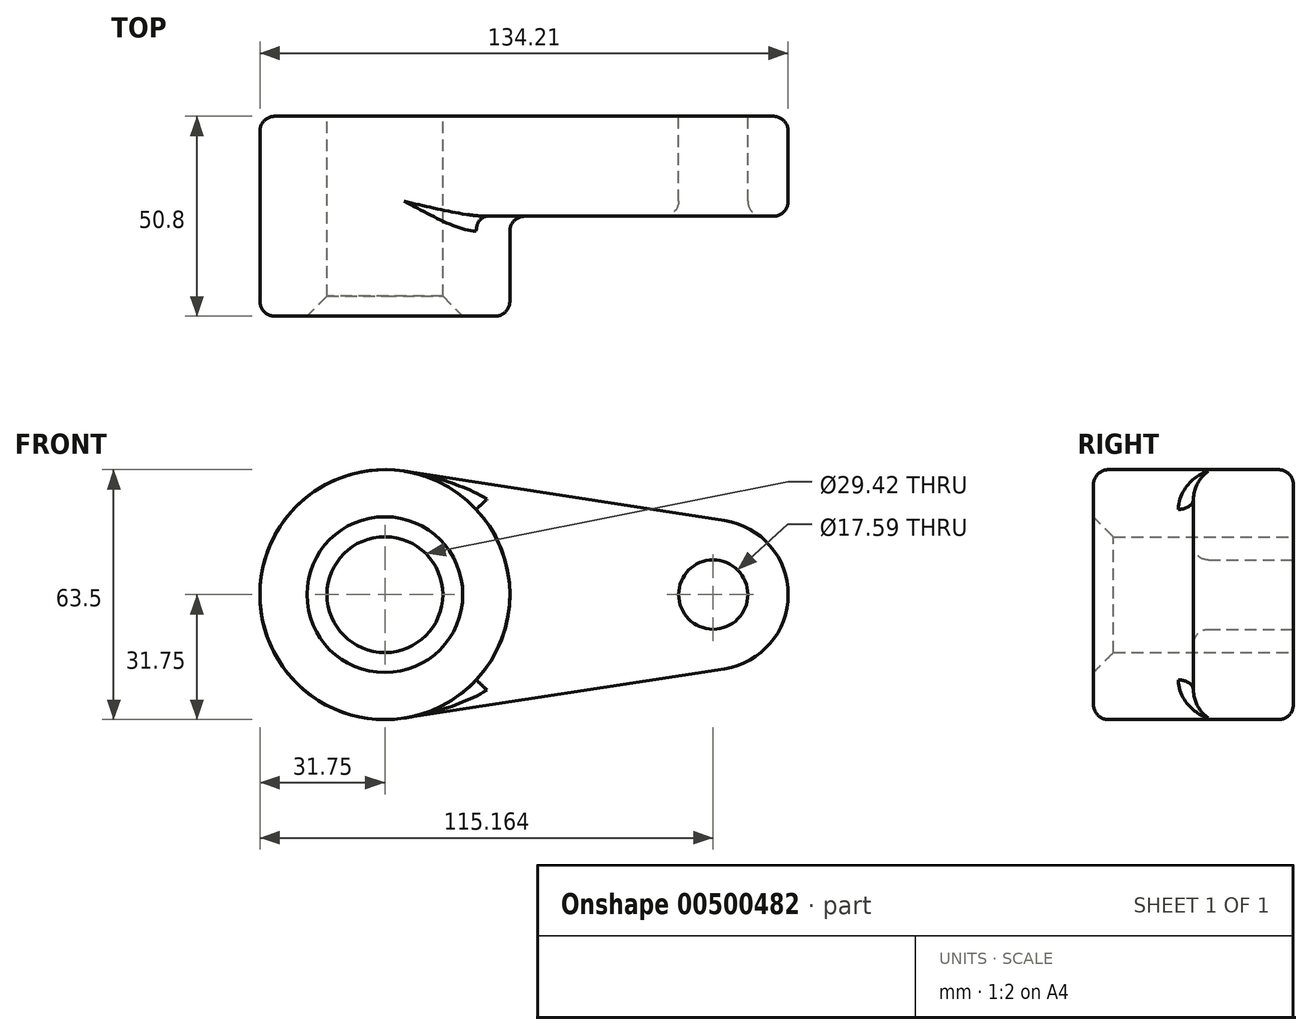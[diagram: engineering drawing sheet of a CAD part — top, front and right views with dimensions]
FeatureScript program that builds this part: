
annotation { "Feature Type Name" : "Feature", "Feature Type Description" : "" }
export const myFeature = defineFeature(function(context is Context, id is Id, definition is map)
    precondition{}
    {
        {
            var Q0;
            Q0=qCreatedBy(makeId("Front.planeOp"),FACE);
            var sketch = newSketch(context, id + "F0", { "sketchPlane" : qUnion([Q0])});
            skCircle(sketch, "E0", {"center": v(0, 0) * mm, "radius": 31.75 * mm});
            skCircle(sketch, "E1", {"center": v(83.41, 0) * mm, "radius": 19.05 * mm});
            skLineSegment(sketch, "E2", {"start": v(4.83, 31.38) * mm, "end": v(86.31, 18.83) * mm});
            skLineSegment(sketch, "E3", {"start": v(4.83, -31.38) * mm, "end": v(86.31, -18.83) * mm});
            skCircle(sketch, "E4", {"center": v(0, 0) * mm, "radius": 14.71 * mm});
            skCircle(sketch, "E5", {"center": v(83.41, 0) * mm, "radius": 8.8 * mm});
            skSolve(sketch);
        }
        {
            var Q0;
            Q0 = qSketchRegion(id + "F0", true);
            extrude(context, id + "F1", {"entities" : qUnion([Q0]), "depth" : 25.4 * mm});
        }
        {
            var Q0;
            Q0=makeQuery(id+"F0.imprint","IMPRINT",FACE,{"disambiguationData":[TD([[makeQuery(id+"F0.imprint","IMPRINT",EDGE,{"derivedFrom":sQuery(id+"F0.wireOp",EDGE,"E4")}),-1.0]])]});
            extrude(context, id + "F2", {"entities" : qUnion([Q0]), "operationType" : NewBodyOperationType.ADD, "depth" : 50.8 * mm});
        }
        {
            var Q0;
            {var subQ0=sQuery(id+"F0.wireOp",EDGE,"E0");Q0=makeQuery(id+"F2.boolean.opBoolean","INTERSECT",EDGE,{"derivedFrom":[makeQuery(id+"F1.opExtrude","CAP_FACE",FACE,{"disambiguationData":[OSD([subQ0,sQuery(id+"F0.wireOp",EDGE,"E1"),sQuery(id+"F0.wireOp",EDGE,"E2"),sQuery(id+"F0.wireOp",EDGE,"E3"),sQuery(id+"F0.wireOp",EDGE,"E4"),sQuery(id+"F0.wireOp",EDGE,"E5")])],"isStart":false}),makeQuery(id+"F2.opExtrude","SWEPT_FACE",FACE,{"disambiguationData":[OSD([subQ0])]})]});}
            var Q1;
            Q1=makeQuery(id+"F2.opExtrude","CAP_EDGE",EDGE,{"disambiguationData":[OSD([sQuery(id+"F0.wireOp",EDGE,"E0")])],"isStart":false});
            var Q2;
            Q2=makeQuery(id+"F1.opExtrude","CAP_EDGE",EDGE,{"disambiguationData":[OSD([sQuery(id+"F0.wireOp",EDGE,"E3")])],"isStart":false});
            var Q3;
            Q3=makeQuery(id+"F1.opExtrude","CAP_EDGE",EDGE,{"disambiguationData":[OSD([sQuery(id+"F0.wireOp",EDGE,"E3")])],"isStart":true});
            var Q4;
            Q4=makeQuery(id+"F1.opExtrude","CAP_EDGE",EDGE,{"disambiguationData":[OSD([sQuery(id+"F0.wireOp",EDGE,"E5")])],"isStart":false});
            fillet(context, id + "F3", {"entities" : qUnion([Q0, Q1, Q2, Q3, Q4]), "radius" : 3.8 * mm, "tangentPropagation" : true, "allowEdgeOverflow" : false});
        }
        {
            var Q0;
            Q0=makeQuery(id+"F2.opExtrude","CAP_EDGE",EDGE,{"disambiguationData":[OSD([sQuery(id+"F0.wireOp",EDGE,"E4")])],"isStart":false});
            chamfer(context, id + "F4", {"entities" : qUnion([Q0]), "width" : 5.08 * mm, "tangentPropagation" : true});
        }
    });
